# Revit family: MSV-F2_DN15-DN150_PN16_RFA
name_source: partatom
category: Pipe Accessories
units: mm (PartAtom-declared; Revit-internal decimal feet)

## family parameters
Always vertical = Yes
Cut with Voids When Loaded = No
Part Type = Valve - Breaks Into
Round Connector Dimension = Use Diameter
Shared = No
Work Plane-Based = No

## types (11) — shared parameters
Connection = Flanges
D4 = 26 mm
D_1_3 = 10 mm
D_S = 26 mm
D_S1 = 27 mm
H9 = 5 mm
IfcExportAs = IfcValveType
IfcExportType = MSV-F2
L2D_Min = 30 mm
LOD 200 = No
LOD 350 = Yes
Manufacturer = Danfoss
Max Flow Temperature = 130 °C
Max Pressure Drop = 1.5 (bar)
Nominal Pressure = 16 bar
R = 50 mm
R10 = 24 mm
R12 = 10 mm
R_C_1 = 26 mm
T_1 = 11 mm
URL = https://store.danfoss.com
Valve Body Material = Danfoss Cast Iron
W2 = 15 mm
W2D = 15 mm

## per-type parameters (varying)
- MSV-F2_DN15_PN16_003Z1085: A=78 mm; A_1=0 mm; A_2=40 mm; A_3=19 mm; A_4=18 mm; A_5=14 mm; A_6=10 mm; A_7=39 mm; CenSd=7 mm; CenSd_RN_6=1 mm; D=15 mm; D4_1=13 mm; D_1=13 mm; D_1_2=10 mm; D_2=18 mm; D_3=15 mm; D_5=36 mm; Description=MSV-F2_DN15_PN16; E=30 mm; EE=4 mm; EE__ve=-4 mm  [stored -0.0131234 ft]; E__ve=-30 mm  [stored -0.0984252 ft]; H1=88 mm; H2=8 mm; H2_1=5 mm; H3=10 mm; H4=33 mm; H5=19 mm; H5__ve=-19 mm  [stored -0.062336 ft]; H6=38 mm; H6__ve=-38 mm; H8=5 mm; H8_1=3 mm; HH_1=12 mm; HH_2=7 mm; HR=-48 mm  [stored -0.15748 ft]; H_10=15 mm; H_S=12 mm; H_TP=5 mm; H_TP3=10 mm; H_TP_2=10 mm; Kvs=3.1 m³/h; L2=27 mm; L2__ve=-27 mm; LSS=8 mm; L_1=38 mm; L_2=92 mm; Model=003Z1085; R1=48 mm; R11=10 mm; R13=12 mm; R14=7 mm; R3=25 mm; R4=13 mm; R5=18 mm; R6=18 mm; R7=14 mm; R8=12 mm; R9=19 mm; RN=1 mm; R_14=1 mm; R_C=35 mm; S1=2 mm; S1__ve=-2 mm  [stored -0.00656168 ft]; S2=12 mm; S22=8 mm; S22_2=20 mm; S2_2=10 mm; S2_2_2=5 mm; S2_3=11 mm; S2_3_1=12 mm; S2__ve=-12 mm; SW_1=26 mm; TD=95 mm; TH=136 mm; TL=130 mm; TP_Front=Yes; TP_Top=No; TP_Top Big=No; T_2=16 mm; V_1=13 mm; V_1_1=5 mm; V_2=39 mm; V_A=50 mm; W1=12 mm; W_1=12 mm; W_TP=57 mm; W_TP_2=48 mm; Weight=2.30 kg; XX=26 mm; X_2=8 mm; X_2_2=25 mm; ZZ=34 mm; ZZ_1=80 mm; Z_4=15 mm
- MSV-F2_DN20_PN16_003Z1086: A=78 mm; A_1=0 mm; A_2=40 mm; A_3=19 mm; A_4=18 mm; A_5=14 mm; A_6=15 mm; A_7=39 mm; CenSd=8 mm; CenSd_RN_6=5 mm; D=20 mm; D4_1=15 mm; D_1=13 mm; D_1_2=10 mm; D_2=18 mm; D_3=15 mm; D_5=33 mm; Description=MSV-F2_DN20_PN16; E=25 mm; EE=9 mm; EE__ve=-9 mm  [stored -0.0295276 ft]; E__ve=-25 mm  [stored -0.082021 ft]; H1=90 mm; H2=7 mm; H2_1=5 mm; H3=10 mm; H4=35 mm; H5=19 mm; H5__ve=-19 mm  [stored -0.062336 ft]; H6=38 mm; H6__ve=-38 mm; H8=5 mm; H8_1=3 mm; HH_1=12 mm; HH_2=7 mm; HR=9 mm; H_10=15 mm; H_S=12 mm; H_TP=53 mm; H_TP3=10 mm; H_TP_2=5 mm; Kvs=6.3 m³/h; L2=27 mm; L2__ve=-27 mm; LSS=8 mm; L_1=45 mm; L_2=105 mm; Model=003Z1086; R1=53 mm; R11=10 mm; R13=2 mm; R14=10 mm; R3=30 mm; R4=15 mm; R5=17 mm; R6=19 mm; R7=15 mm; R8=11 mm; R9=19 mm; RN=6 mm; R_14=1 mm; R_C=35 mm; S1=2 mm; S1__ve=-2 mm  [stored -0.00656168 ft]; S2=14 mm; S22=8 mm; S22_2=20 mm; S2_2=10 mm; S2_2_2=5 mm; S2_3=13 mm; S2_3_1=12 mm; S2__ve=-14 mm  [stored -0.0459318 ft]; SW_1=26 mm; TD=105 mm; TH=143 mm; TL=150 mm; TP_Front=No; TP_Top=Yes; TP_Top Big=No; T_2=16 mm; V_1=15 mm; V_1_1=5 mm; V_2=39 mm; V_A=50 mm; W1=12 mm; W_1=12 mm; W_TP=10 mm; W_TP_2=10 mm; Weight=2.90 kg; XX=26 mm; X_2=12 mm; X_2_2=25 mm; ZZ=34 mm; ZZ_1=80 mm; Z_4=15 mm
- MSV-F2_DN25_PN16_003Z1087: A=78 mm; A_1=1 mm; A_2=40 mm; A_3=27 mm; A_4=18 mm; A_5=14 mm; A_6=13 mm; A_7=39 mm; CenSd=7 mm; CenSd_RN_6=6 mm; D=25 mm; D4_1=19 mm; D_1=18 mm; D_1_2=13 mm; D_2=20 mm; D_3=16 mm; D_5=41 mm; Description=MSV-F2_DN25_PN16; E=35 mm; EE=8 mm; EE__ve=-8 mm; E__ve=-35 mm; H1=100 mm; H2=16 mm; H2_1=7 mm; H3=5 mm; H4=33 mm; H5=19 mm; H5__ve=-19 mm  [stored -0.062336 ft]; H6=39 mm; H6__ve=-39 mm; H8=5 mm; H8_1=3 mm; HH_1=12 mm; HH_2=6 mm; HR=9 mm; H_10=15 mm; H_S=18 mm; H_TP=58 mm; H_TP3=10 mm; H_TP_2=10 mm; Kvs=9.0 m³/h; L2=13 mm; L2__ve=-13 mm; LSS=5 mm; L_1=50 mm; L_2=110 mm; Model=003Z1087; R1=58 mm; R11=13 mm; R13=2 mm; R14=2 mm; R3=36 mm; R4=19 mm; R5=21 mm; R6=25 mm; R7=27 mm; R8=10 mm; R9=25 mm; RN=7 mm; R_14=1 mm; R_C=35 mm; S1=3 mm; S1__ve=-3 mm; S2=13 mm; S22=13 mm; S22_2=20 mm; S2_2=12 mm; S2_2_2=5 mm; S2_3=13 mm; S2_3_1=19 mm; S2__ve=-13 mm; SW_1=26 mm; TD=115 mm; TH=158 mm; TL=160 mm; TP_Front=No; TP_Top=Yes; TP_Top Big=No; T_2=16 mm; V_1=19 mm; V_1_1=20 mm; V_2=39 mm; V_A=45 mm; W1=12 mm; W_1=12 mm; W_TP=10 mm; W_TP_2=10 mm; Weight=3.80 kg; XX=26 mm; X_2=25 mm; X_2_2=30 mm; ZZ=44 mm; ZZ_1=65 mm; Z_4=22 mm
- MSV-F2_DN32_PN16_003Z1088: A=78 mm; A_1=0 mm; A_2=40 mm; A_3=26 mm; A_4=18 mm; A_5=14 mm; A_6=11 mm; A_7=39 mm; CenSd=7 mm; CenSd_RN_6=6 mm; D=32 mm; D4_1=24 mm; D_1=15 mm; D_1_2=11 mm; D_2=20 mm; D_3=16 mm; D_5=53 mm; Description=MSV-F2_DN32_PN16; E=15 mm; EE=33 mm; EE__ve=-33 mm; E__ve=-15 mm  [stored -0.0492126 ft]; H1=100 mm; H2=9 mm; H2_1=6 mm; H3=9 mm; H4=32 mm; H5=19 mm; H5__ve=-19 mm  [stored -0.062336 ft]; H6=46 mm; H6__ve=-46 mm; H8=5 mm; H8_1=3 mm; HH_1=11 mm; HH_2=6 mm; HR=9 mm; H_10=15 mm; H_S=13 mm; H_TP=70 mm; H_TP3=10 mm; H_TP_2=10 mm; Kvs=15.5 m³/h; L2=15 mm; L2__ve=-15 mm  [stored -0.0492126 ft]; LSS=5 mm; L_1=50 mm; L_2=130 mm; Model=003Z1088; R1=70 mm; R11=10 mm; R13=2 mm; R14=15 mm; R3=40 mm; R4=24 mm; R5=26 mm; R6=26 mm; R7=18 mm; R8=12 mm; R9=26 mm; RN=7 mm; R_14=1 mm; R_C=35 mm; S1=3 mm; S1__ve=-3 mm; S2=17 mm; S22=8 mm; S22_2=26 mm; S2_2=13 mm; S2_2_2=5 mm; S2_3=12 mm; S2_3_1=18 mm; S2__ve=-17 mm; SW_1=26 mm; TD=140 mm; TH=170 mm; TL=180 mm; TP_Front=No; TP_Top=Yes; TP_Top Big=No; T_2=16 mm; V_1=24 mm; V_1_1=20 mm; V_2=38 mm; V_A=40 mm; W1=12 mm; W_1=12 mm; W_TP=10 mm; W_TP_2=10 mm; Weight=5.60 kg; XX=35 mm; X_2=27 mm; X_2_2=24 mm; ZZ=48 mm; ZZ_1=65 mm; Z_4=20 mm
- MSV-F2_DN40_PN16_003Z1089: A=78 mm; A_1=0 mm; A_2=45 mm; A_3=32 mm; A_4=18 mm; A_5=14 mm; A_6=11 mm; A_7=39 mm; CenSd=7 mm; CenSd_RN_6=6 mm; D=40 mm; D4_1=28 mm; D_1=15 mm; D_1_2=11 mm; D_2=19 mm; D_3=15 mm; D_5=66 mm; Description=MSV-F2_DN40_PN16; E=54 mm; EE=5 mm; EE__ve=-5 mm  [stored -0.0164042 ft]; E__ve=-54 mm; H1=125 mm; H2=16 mm; H2_1=6 mm; H3=17 mm; H4=33 mm; H5=19 mm; H5__ve=-19 mm  [stored -0.062336 ft]; H6=45 mm; H6__ve=-45 mm; H8=4 mm; H8_1=3 mm; HH_1=12 mm; HH_2=6 mm; HR=9 mm; H_10=15 mm; H_S=17 mm; H_TP=75 mm; H_TP3=10 mm; H_TP_2=10 mm; Kvs=32.3 m³/h; L2=10 mm; L2__ve=-10 mm  [stored -0.0328084 ft]; LSS=6 mm; L_1=63 mm; L_2=137 mm; Model=003Z1089; R1=75 mm; R11=10 mm; R13=2 mm; R14=15 mm; R3=45 mm; R4=28 mm; R5=33 mm; R6=31 mm; R7=17 mm; R8=10 mm; R9=32 mm; RN=7 mm; R_14=9 mm; R_C=28 mm; S1=3 mm; S1__ve=-3 mm; S2=17 mm; S22=12 mm; S22_2=35 mm; S2_2=14 mm; S2_2_2=5 mm; S2_3=18 mm; S2_3_1=21 mm; S2__ve=-17 mm; SW_1=25 mm; TD=150 mm; TH=200 mm; TL=200 mm; TP_Front=No; TP_Top=Yes; TP_Top Big=No; T_2=16 mm; V_1=28 mm; V_1_1=20 mm; V_2=38 mm; V_A=50 mm; W1=12 mm; W_1=12 mm; W_TP=11 mm; W_TP_2=10 mm; Weight=7.20 kg; XX=33 mm; X_2=22 mm; X_2_2=30 mm; ZZ=59 mm; ZZ_1=92 mm; Z_4=25 mm
- MSV-F2_DN50_PN16_003Z1061: A=78 mm; A_1=2 mm; A_2=45 mm; A_3=41 mm; A_4=18 mm; A_5=14 mm; A_6=10 mm; A_7=39 mm; CenSd=7 mm; CenSd_RN_6=1 mm; D=50 mm; D4_1=35 mm; D_1=15 mm; D_1_2=10 mm; D_2=20 mm; D_3=13 mm; D_5=77 mm; Description=MSV-F2_DN50_PN16; E=15 mm; EE=48 mm; EE__ve=-48 mm  [stored -0.15748 ft]; E__ve=-15 mm  [stored -0.0492126 ft]; H1=125 mm; H2=27 mm; H2_1=15 mm; H3=8 mm; H4=32 mm; H5=15 mm; H5__ve=-15 mm  [stored -0.0492126 ft]; H6=48 mm; H6__ve=-48 mm  [stored -0.15748 ft]; H8=6 mm; H8_1=3 mm; HH_1=10 mm; HH_2=7 mm; HR=9 mm; H_10=15 mm; H_S=18 mm; H_TP=10 mm; H_TP3=92 mm; H_TP_2=83 mm; Kvs=53.8 m³/h; L2=6 mm; L2__ve=-6 mm; LSS=8 mm; L_1=67 mm; L_2=163 mm; Model=003Z1061; R1=83 mm; R11=10 mm; R13=2 mm; R14=15 mm; R3=53 mm; R4=35 mm; R5=39 mm; R6=41 mm; R7=41 mm; R8=13 mm; R9=41 mm; RN=1 mm; R_14=9 mm; R_C=35 mm; S1=3 mm; S1__ve=-3 mm; S2=20 mm; S22=13 mm; S22_2=35 mm; S2_2=13 mm; S2_2_2=5 mm; S2_3=18 mm; S2_3_1=22 mm; S2__ve=-20 mm; SW_1=26 mm; TD=165 mm; TH=208 mm; TL=230 mm; TP_Front=No; TP_Top=Yes; TP_Top Big=Yes; T_2=16 mm; V_1=35 mm; V_1_1=5 mm; V_2=38 mm; V_A=60 mm; W1=12 mm; W_1=12 mm; W_TP=11 mm; W_TP_2=10 mm; Weight=9.40 kg; XX=42 mm; X_2=40 mm; X_2_2=42 mm; ZZ=65 mm; ZZ_1=100 mm; Z_4=23 mm
- MSV-F2_DN65_PN16_003Z1062: A=140 mm; A_1=10 mm; A_2=80 mm; A_3=60 mm; A_4=35 mm; A_5=28 mm; A_6=23 mm; A_7=70 mm; CenSd=7 mm; CenSd_RN_6=6 mm; D=65 mm; D4_1=39 mm; D_1=40 mm; D_1_2=23 mm; D_2=33 mm; D_3=28 mm; D_5=86 mm; Description=MSV-F2_DN65_PN16; E=35 mm; EE=32 mm; EE__ve=-32 mm; E__ve=-35 mm; H1=187 mm; H2=42 mm; H2_1=19 mm; H3=25 mm; H4=46 mm; H5=24 mm; H5__ve=-24 mm; H6=54 mm; H6__ve=-54 mm; H8=8 mm; H8_1=3 mm; HH_1=12 mm; HH_2=10 mm; HR=9 mm; H_10=15 mm; H_S=25 mm; H_TP=93 mm; H_TP3=84 mm; H_TP_2=10 mm; Kvs=93.4 m³/h; L2=20 mm; L2__ve=-20 mm; LSS=25 mm; L_1=97 mm; L_2=193 mm; Model=003Z1062; R1=93 mm; R11=23 mm; R13=2 mm; R14=13 mm; R3=62 mm; R4=39 mm; R5=43 mm; R6=55 mm; R7=60 mm; R8=15 mm; R9=46 mm; RN=7 mm; R_14=9 mm; R_C=35 mm; S1=3 mm; S1__ve=-3 mm; S2=17 mm; S22=22 mm; S22_2=42 mm; S2_2=12 mm; S2_2_2=5 mm; S2_3=17 mm; S2_3_1=17 mm; S2__ve=-17 mm; SW_1=26 mm; TD=185 mm; TH=280 mm; TL=290 mm; TP_Front=No; TP_Top=Yes; TP_Top Big=Yes; T_2=10 mm; V_1=39 mm; V_1_1=20 mm; V_2=38 mm; V_A=94 mm; W1=16 mm; W_1=12 mm; W_TP=11 mm; W_TP_2=10 mm; Weight=17.00 kg; XX=42 mm; X_2=55 mm; X_2_2=50 mm; ZZ=77 mm; ZZ_1=144 mm; Z_4=35 mm
- MSV-F2_DN80_PN16_003Z1063: A=140 mm; A_1=13 mm; A_2=80 mm; A_3=70 mm; A_4=35 mm; A_5=28 mm; A_6=24 mm; A_7=70 mm; CenSd=7 mm; CenSd_RN_6=1 mm; D=80 mm; D4_1=48 mm; D_1=48 mm; D_1_2=24 mm; D_2=33 mm; D_3=27 mm; D_5=106 mm; Description=MSV-F2_DN80_PN16; E=41 mm; EE=30 mm; EE__ve=-30 mm  [stored -0.0984252 ft]; E__ve=-41 mm; H1=207 mm; H2=56 mm; H2_1=24 mm; H3=25 mm; H4=48 mm; H5=22 mm; H5__ve=-22 mm; H6=52 mm; H6__ve=-52 mm; H8=13 mm; H8_1=15 mm; HH_1=14 mm; HH_2=12 mm; HR=9 mm; H_10=15 mm; H_S=30 mm; H_TP=40 mm; H_TP3=109 mm; H_TP_2=100 mm; Kvs=122.3 m³/h; L2=15 mm; L2__ve=-15 mm  [stored -0.0492126 ft]; LSS=21 mm; L_1=106 mm; L_2=204 mm; Model=003Z1063; R1=100 mm; R11=25 mm; R13=2 mm; R14=15 mm; R3=69 mm; R4=48 mm; R5=53 mm; R6=70 mm; R7=70 mm; R8=18 mm; R9=58 mm; RN=1 mm; R_14=7 mm; R_C=62 mm; S1=3 mm; S1__ve=-3 mm; S2=19 mm; S22=35 mm; S22_2=40 mm; S2_2=10 mm; S2_2_2=5 mm; S2_3=20 mm; S2_3_1=20 mm; S2__ve=-19 mm  [stored -0.062336 ft]; SW_1=26 mm; TD=200 mm; TH=307 mm; TL=310 mm; TP_Front=No; TP_Top=No; TP_Top Big=Yes; T_2=16 mm; V_1=48 mm; V_1_1=20 mm; V_2=38 mm; V_A=83 mm; W1=30 mm; W_1=34 mm; W_TP=11 mm; W_TP_2=10 mm; Weight=21.00 kg; XX=42 mm; X_2=48 mm; X_2_2=50 mm; ZZ=84 mm; ZZ_1=167 mm; Z_4=65 mm
- MSV-F2_DN100_PN16_003Z1064: A=140 mm; A_1=13 mm; A_2=75 mm; A_3=90 mm; A_4=35 mm; A_5=28 mm; A_6=26 mm; A_7=70 mm; CenSd=7 mm; CenSd_RN_6=1 mm; D=100 mm; D4_1=60 mm; D_1=60 mm; D_1_2=26 mm; D_2=33 mm; D_3=27 mm; D_5=132 mm; Description=MSV-F2_DN100_PN16; E=50 mm; EE=42 mm; EE__ve=-42 mm; E__ve=-50 mm  [stored -0.164042 ft]; H1=223 mm; H2=53 mm; H2_1=26 mm; H3=26 mm; H4=49 mm; H5=27 mm; H5__ve=-27 mm; H6=50 mm; H6__ve=-50 mm  [stored -0.164042 ft]; H8=13 mm; H8_1=13 mm; HH_1=13 mm; HH_2=9 mm; HR=9 mm; H_10=3 mm; H_S=35 mm; H_TP=40 mm; H_TP3=119 mm; H_TP_2=110 mm; Kvs=200.0 m³/h; L2=15 mm; L2__ve=-15 mm  [stored -0.0492126 ft]; LSS=18 mm; L_1=120 mm; L_2=230 mm; Model=003Z1064; R1=110 mm; R11=24 mm; R13=1 mm; R14=15 mm; R3=81 mm; R4=60 mm; R5=66 mm; R6=85 mm; R7=90 mm; R8=23 mm; R9=70 mm; RN=1 mm; R_14=9 mm; R_C=50 mm; S1=3 mm; S1__ve=-3 mm; S2=21 mm; S22=42 mm; S22_2=35 mm; S2_2=11 mm; S2_2_2=5 mm; S2_3=16 mm; S2_3_1=25 mm; S2__ve=-21 mm; SW_1=26 mm; TD=220 mm; TH=333 mm; TL=350 mm; TP_Front=No; TP_Top=No; TP_Top Big=Yes; T_2=16 mm; V_1=60 mm; V_1_1=5 mm; V_2=38 mm; V_A=80 mm; W1=22 mm; W_1=22 mm; W_TP=11 mm; W_TP_2=10 mm; Weight=32.00 kg; XX=0 mm; X_2=80 mm; X_2_2=60 mm; ZZ=107 mm; ZZ_1=65 mm; Z_4=70 mm
- MSV-F2_DN125_PN16_003Z1065: A=140 mm; A_1=10 mm; A_2=80 mm; A_3=98 mm; A_4=32 mm; A_5=28 mm; A_6=25 mm; A_7=70 mm; CenSd=7 mm; CenSd_RN_6=1 mm; D=125 mm; D4_1=75 mm; D_1=75 mm; D_1_2=25 mm; D_2=33 mm; D_3=28 mm; D_5=165 mm; Description=MSV-F2_DN125_PN16; E=63 mm; EE=35 mm; EE__ve=-35 mm; E__ve=-63 mm; H1=252 mm; H2=57 mm; H2_1=30 mm; H3=52 mm; H4=45 mm; H5=23 mm; H5__ve=-23 mm; H6=50 mm; H6__ve=-50 mm  [stored -0.164042 ft]; H8=16 mm; H8_1=16 mm; HH_1=13 mm; HH_2=9 mm; HR=-1 mm  [stored -0.00328084 ft]; H_10=3 mm; H_S=40 mm; H_TP=40 mm; H_TP3=134 mm; H_TP_2=125 mm; Kvs=304.4 m³/h; L2=50 mm; L2__ve=-50 mm  [stored -0.164042 ft]; LSS=38 mm; L_1=144 mm; L_2=256 mm; Model=003Z1065; R1=125 mm; R11=25 mm; R13=2 mm; R14=15 mm; R3=95 mm; R4=75 mm; R5=83 mm; R6=95 mm; R7=98 mm; R8=29 mm; R9=84 mm; RN=1 mm; R_14=7 mm; R_C=60 mm; S1=3 mm; S1__ve=-3 mm; S2=23 mm; S22=31 mm; S22_2=42 mm; S2_2=13 mm; S2_2_2=9 mm; S2_3=25 mm; S2_3_1=21 mm; S2__ve=-23 mm; SW_1=26 mm; TD=250 mm; TH=377 mm; TL=400 mm; TP_Front=No; TP_Top=No; TP_Top Big=Yes; T_2=16 mm; V_1=75 mm; V_1_1=5 mm; V_2=38 mm; V_A=100 mm; W1=40 mm; W_1=40 mm; W_TP=11 mm; W_TP_2=10 mm; Weight=44.00 kg; XX=0 mm; X_2=82 mm; X_2_2=50 mm; ZZ=108 mm; ZZ_1=65 mm; Z_4=60 mm
- MSV-F2_DN150_PN16_003Z1066: A=140 mm; A_1=22 mm; A_2=80 mm; A_3=112 mm; A_4=27 mm; A_5=28 mm; A_6=25 mm; A_7=70 mm; CenSd=7 mm; CenSd_RN_6=1 mm; D=150 mm; D4_1=90 mm; D_1=77 mm; D_1_2=25 mm; D_2=32 mm; D_3=26 mm; D_5=198 mm; Description=MSV-F2_DN150_PN16; E=55 mm; EE=56 mm; EE__ve=-56 mm; E__ve=-55 mm; H1=248 mm; H2=35 mm; H2_1=12 mm; H3=46 mm; H4=45 mm; H5=24 mm; H5__ve=-24 mm; H6=53 mm; H6__ve=-53 mm; H8=14 mm; H8_1=15 mm; HH_1=13 mm; HH_2=8 mm; HR=9 mm; H_10=3 mm; H_S=40 mm; H_TP=40 mm; H_TP3=151 mm; H_TP_2=143 mm; Kvs=400.8 m³/h; L2=25 mm; L2__ve=-25 mm  [stored -0.082021 ft]; LSS=50 mm; L_1=176 mm; L_2=304 mm; Model=003Z1066; R1=143 mm; R11=24 mm; R13=2 mm; R14=15 mm; R3=109 mm; R4=90 mm; R5=99 mm; R6=112 mm; R7=110 mm; R8=76 mm; R9=95 mm; RN=1 mm; R_14=9 mm; R_C=60 mm; S1=3 mm; S1__ve=-3 mm; S2=23 mm; S22=60 mm; S22_2=42 mm; S2_2=13 mm; S2_2_2=7 mm; S2_3=7 mm; S2_3_1=21 mm; S2__ve=-23 mm; SW_1=26 mm; TD=285 mm; TH=391 mm; TL=480 mm; TP_Front=No; TP_Top=No; TP_Top Big=Yes; T_2=16 mm; V_1=90 mm; V_1_1=5 mm; V_2=38 mm; V_A=120 mm; W1=37 mm; W_1=33 mm; W_TP=11 mm; W_TP_2=10 mm; Weight=56.50 kg; XX=0 mm; X_2=80 mm; X_2_2=70 mm; ZZ=133 mm; ZZ_1=65 mm; Z_4=50 mm

note: [stored X ft] marks values corroborated as IEEE doubles in the binary element streams (Revit-internal decimal feet)

## geometry (parser evidence)
native form markers: Sweep x6
no freeform markers — native parametric forms only
